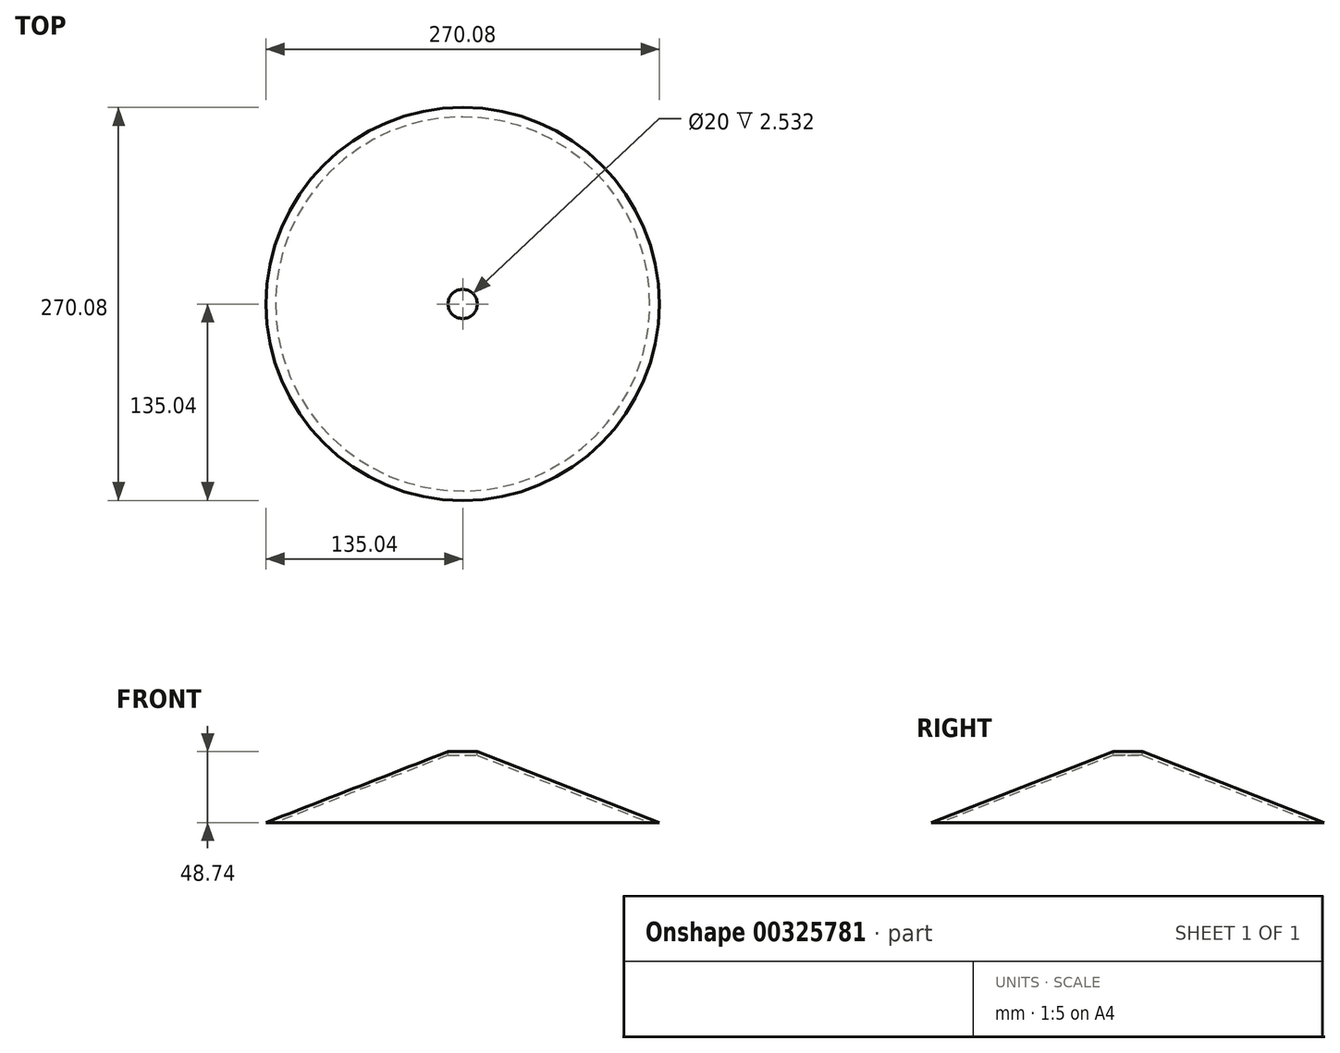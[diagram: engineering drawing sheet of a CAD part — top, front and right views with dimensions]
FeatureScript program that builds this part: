
annotation { "Feature Type Name" : "Feature", "Feature Type Description" : "" }
export const myFeature = defineFeature(function(context is Context, id is Id, definition is map)
    precondition{}
    {
        {
            var Q0;
            Q0=qCreatedBy(makeId("Front.planeOp"),FACE);
            var sketch = newSketch(context, id + "F0", { "sketchPlane" : qUnion([Q0])});
            skLineSegment(sketch, "E0", {"start": v(159.15, 72.93) * mm, "end": v(10, 131.07) * mm});
            skLineSegment(sketch, "E1", {"start": v(0, 131.07) * mm, "end": v(10, 131.07) * mm});
            skLineSegment(sketch, "E2", {"start": v(0, 128.54) * mm, "end": v(10, 128.54) * mm});
            skLineSegment(sketch, "E3", {"start": v(10, 128.54) * mm, "end": v(135.11, 79.77) * mm});
            skLineSegment(sketch, "E4.trimOffspring", {"start": v(0, 128.54) * mm, "end": v(0, 131.07) * mm});
            skLineSegment(sketch, "E5", {"start": v(159.15, 72.93) * mm, "end": v(11.22, 72.93) * mm});
            skLineSegment(sketch, "E6", {"start": v(11.22, 72.93) * mm, "end": v(11.22, 79.63) * mm});
            skLineSegment(sketch, "E7", {"start": v(11.22, 79.63) * mm, "end": v(135.11, 79.77) * mm});
            skSolve(sketch);
        }
        {
            var Q0;
            Q0=makeQuery(id+"F0.imprint","IMPRINT",FACE,{"disambiguationData":[TD([[makeQuery(id+"F0.imprint","IMPRINT",EDGE,{"derivedFrom":sQuery(id+"F0.wireOp",EDGE,"E0")}),1.0]])]});
            var Q1;
            Q1=sQuery(id+"F0.wireOp",EDGE,"E4.trimOffspring");
            revolve(context, id + "F1", {"entities" : qUnion([Q0]), "axis" : qUnion([Q1]), "revolveType" : RevolveType.FULL});
        }
        {
            var Q0;
            Q0=makeQuery(id+"F1.opRevolve","SWEPT_FACE",FACE,{"disambiguationData":[OSD([sQuery(id+"F0.wireOp",EDGE,"E1")])]});
            extrude(context, id + "F2", {"entities" : qUnion([Q0]), "operationType" : NewBodyOperationType.REMOVE, "oppositeDirection" : true, "depth" : 25.4 * mm});
        }
        {
            var Q0;
            Q0=makeQuery(id+"F1.opRevolve","SWEPT_FACE",FACE,{"disambiguationData":[OSD([sQuery(id+"F0.wireOp",EDGE,"E5")])]});
            extrude(context, id + "F3", {"entities" : qUnion([Q0]), "operationType" : NewBodyOperationType.REMOVE, "oppositeDirection" : true, "depth" : 9.4 * mm});
        }
    });
